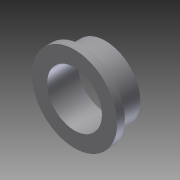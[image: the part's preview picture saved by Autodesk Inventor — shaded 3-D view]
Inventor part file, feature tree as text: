
AUTODESK INVENTOR PART (.ipt)
format: ipt  version: 2013 (Build 170138000, 138)  size: 92,672 bytes
history: native  units: in
note: dims shown in document units (in); Inventor stores cm internally (conversion verified against a paired STEP export)
features: sketch x3, extrude x2, hole x1
ambient origin geometry x8: Origin, YZ Plane, XZ Plane, XY Plane, X Axis, Y Axis, Z Axis, Center Point
bodies: Solid1 (feature_tree)
feature tree (6):
  extrude  "Extrusion1"  Depth=0.039in TaperAngle=0.0deg
  extrude  "Extrusion2"  Depth=0.118in TaperAngle=0.0deg
  hole  "Hole1"  [1 undecoded]
  sketch  "Sketch1"  dims[d0=0.433in d1=0.039in d2=0.0in]
  sketch  "Sketch2"  dims[d3=0.354in d4=0.118in d5=0.0in]
  sketch  "Sketch3"  dims[d6=0.278in d7=0.75in d8=0.375in d9=0.25in d10=0.5635in d11=1.0in d12=0.8108in]
note: 1 required parameter value undecoded (feature->parameter linkage not recoverable at this tier; creation-order binding heuristic only, values carry confidence <= 0.55)
